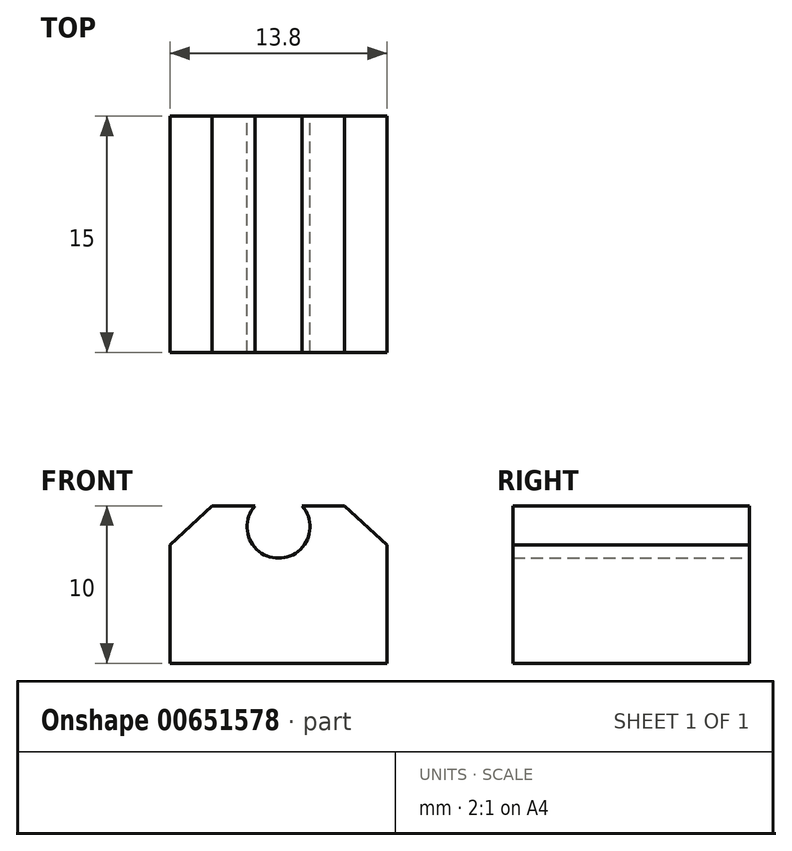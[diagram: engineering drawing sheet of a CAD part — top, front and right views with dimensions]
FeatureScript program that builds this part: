
annotation { "Feature Type Name" : "Feature", "Feature Type Description" : "" }
export const myFeature = defineFeature(function(context is Context, id is Id, definition is map)
    precondition{}
    {
        {
            var Q0;
            Q0=qCreatedBy(makeId("Front.planeOp"),FACE);
            var sketch = newSketch(context, id + "F0", { "sketchPlane" : qUnion([Q0])});
            skLineSegment(sketch, "E0", {"start": v(-4.2, 10) * mm, "end": v(-1.5, 10) * mm});
            skLineSegment(sketch, "E1.MirrorCS", {"start": v(4.2, 10) * mm, "end": v(1.5, 10) * mm});
            skArc(sketch, "E2", {"start": v(-1.5, 10) * mm, "mid": v(0, 6.68) * mm, "end": v(1.5, 10) * mm});
            skLineSegment(sketch, "E3", {"start": v(6.9, 7.5) * mm, "end": v(6.9, 0) * mm});
            skLineSegment(sketch, "E4.MirrorCS", {"start": v(-6.9, 7.5) * mm, "end": v(-6.9, 0) * mm});
            skLineSegment(sketch, "E5", {"start": v(6.9, 7.5) * mm, "end": v(4.2, 10) * mm});
            skLineSegment(sketch, "E6", {"start": v(-4.2, 10) * mm, "end": v(-6.9, 7.5) * mm});
            skLineSegment(sketch, "E7", {"start": v(6.9, 0) * mm, "end": v(-6.9, 0) * mm});
            skSolve(sketch);
        }
        {
            var Q0;
            Q0 = qSketchRegion(id + "F0", true);
            extrude(context, id + "F1", {"entities" : qUnion([Q0]), "depth" : 15 * mm, "offsetDistance" : 25 * mm});
        }
    });
